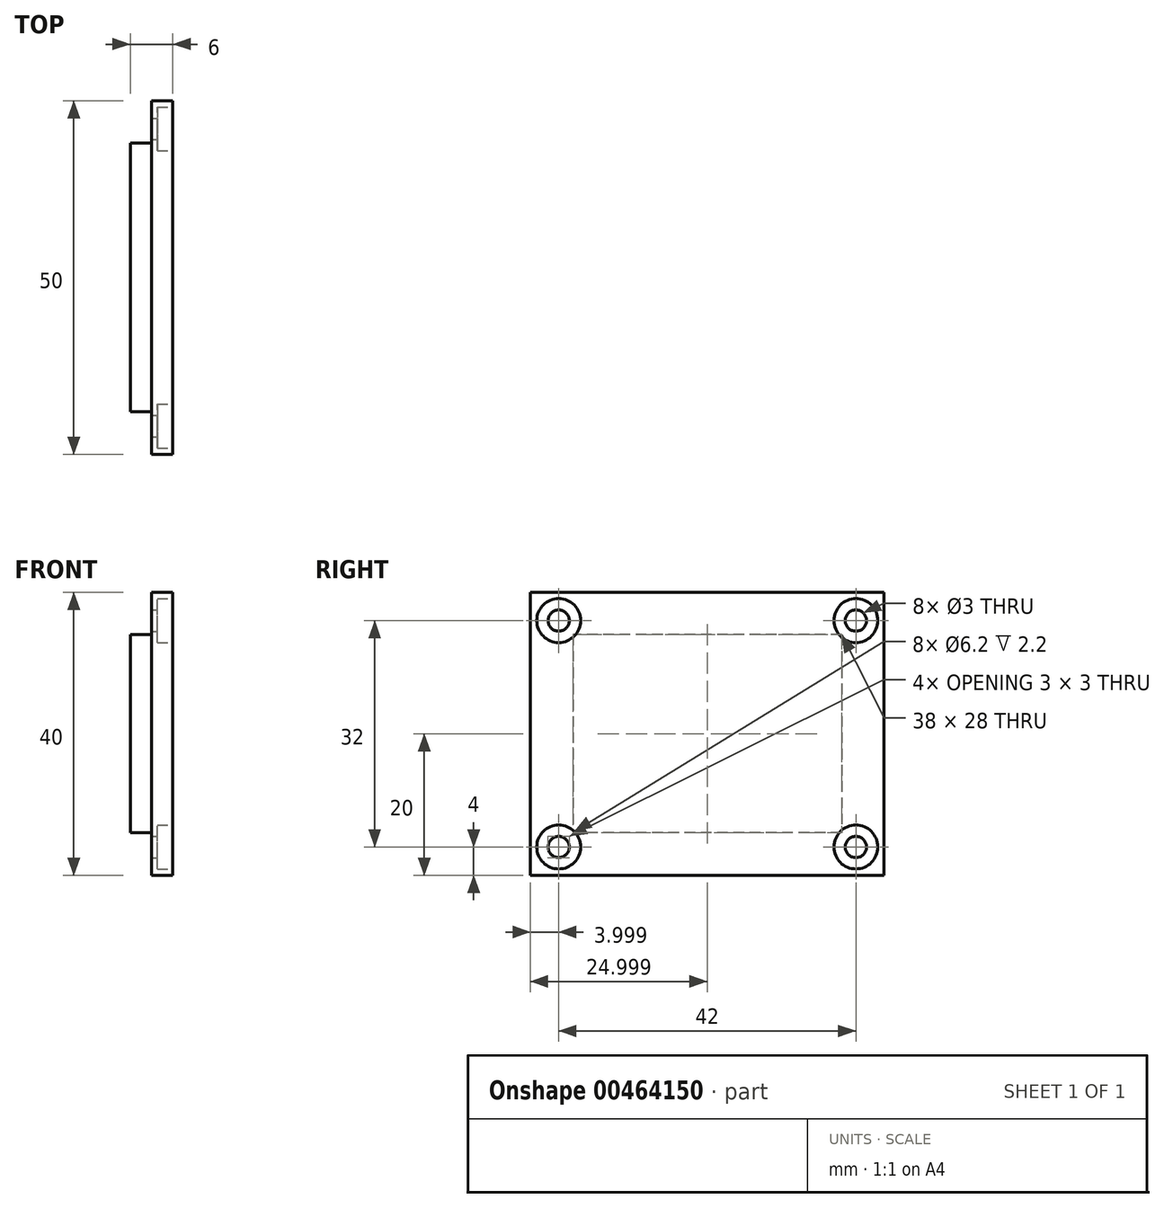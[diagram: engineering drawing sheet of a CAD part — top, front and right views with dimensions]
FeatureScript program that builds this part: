
annotation { "Feature Type Name" : "Feature", "Feature Type Description" : "" }
export const myFeature = defineFeature(function(context is Context, id is Id, definition is map)
    precondition{}
    {
        {
            var Q0;
            Q0=qCreatedBy(makeId("Right.planeOp"),FACE);
            var sketch = newSketch(context, id + "F0", { "sketchPlane" : qUnion([Q0])});
            skLineSegment(sketch, "E0.bottom", {"start": v(1.15, 0) * mm, "end": v(51.15, 0) * mm});
            skLineSegment(sketch, "E0.top", {"start": v(1.15, 40) * mm, "end": v(51.15, 40) * mm});
            skLineSegment(sketch, "E0.left", {"start": v(1.15, 0) * mm, "end": v(1.15, 40) * mm});
            skLineSegment(sketch, "E0.right", {"start": v(51.15, 0) * mm, "end": v(51.15, 40) * mm});
            skSolve(sketch);
        }
        {
            var Q0;
            Q0 = qSketchRegion(id + "F0", true);
            extrude(context, id + "F1", {"entities" : qUnion([Q0]), "depth" : 6 * mm});
        }
        {
            var Q0;
            Q0=makeQuery(id+"F1.opExtrude","CAP_FACE",FACE,{"disambiguationData":[OSD([sQuery(id+"F0.wireOp",EDGE,"E0.bottom"),sQuery(id+"F0.wireOp",EDGE,"E0.top"),sQuery(id+"F0.wireOp",EDGE,"E0.left"),sQuery(id+"F0.wireOp",EDGE,"E0.right")])],"isStart":true});
            var sketch = newSketch(context, id + "F2", { "sketchPlane" : qUnion([Q0])});
            skLineSegment(sketch, "E1.bottom", {"start": v(-45.15, 34) * mm, "end": v(-7.15, 34) * mm});
            skLineSegment(sketch, "E1.top", {"start": v(-45.15, 6) * mm, "end": v(-7.15, 6) * mm});
            skLineSegment(sketch, "E1.left", {"start": v(-45.15, 34) * mm, "end": v(-45.15, 6) * mm});
            skLineSegment(sketch, "E1.right", {"start": v(-7.15, 34) * mm, "end": v(-7.15, 6) * mm});
            skSolve(sketch);
        }
        {
            var Q0;
            Q0=makeQuery(id+"F2.imprint","IMPRINT",FACE,{"disambiguationData":[TD([[makeQuery(id+"F2.imprint","IMPRINT",EDGE,{"derivedFrom":sQuery(id+"F2.wireOp",EDGE,"E1.bottom")}),1.0]])]});
            extrude(context, id + "F3", {"entities" : qUnion([Q0]), "operationType" : NewBodyOperationType.REMOVE, "oppositeDirection" : true, "depth" : 3 * mm});
        }
        {
            var Q0;
            Q0=makeQuery(id+"F1.opExtrude","CAP_FACE",FACE,{"disambiguationData":[OSD([sQuery(id+"F0.wireOp",EDGE,"E0.bottom"),sQuery(id+"F0.wireOp",EDGE,"E0.top"),sQuery(id+"F0.wireOp",EDGE,"E0.left"),sQuery(id+"F0.wireOp",EDGE,"E0.right")])],"isStart":false});
            var sketch = newSketch(context, id + "F4", { "sketchPlane" : qUnion([Q0])});
            skCircle(sketch, "E2", {"center": v(47.15, 36) * mm, "radius": 1.5 * mm});
            skCircle(sketch, "E3", {"center": v(5.15, 36) * mm, "radius": 1.5 * mm});
            skCircle(sketch, "E4", {"center": v(5.15, 4) * mm, "radius": 1.5 * mm});
            skCircle(sketch, "E5", {"center": v(47.15, 4) * mm, "radius": 1.5 * mm});
            skSolve(sketch);
        }
        {
            var Q0;
            Q0 = qSketchRegion(id + "F4", true);
            extrude(context, id + "F5", {"entities" : qUnion([Q0]), "operationType" : NewBodyOperationType.REMOVE, "endBound" : BoundingType.THROUGH_ALL, "oppositeDirection" : true, "depth" : 25 * mm});
        }
        {
            var Q0;
            Q0=makeQuery(id+"F1.opExtrude","CAP_FACE",FACE,{"disambiguationData":[OSD([sQuery(id+"F0.wireOp",EDGE,"E0.bottom"),sQuery(id+"F0.wireOp",EDGE,"E0.top"),sQuery(id+"F0.wireOp",EDGE,"E0.left"),sQuery(id+"F0.wireOp",EDGE,"E0.right")])],"isStart":false});
            var sketch = newSketch(context, id + "F6", { "sketchPlane" : qUnion([Q0])});
            skCircle(sketch, "E6", {"center": v(5.15, 36) * mm, "radius": 3.1 * mm});
            skCircle(sketch, "E7", {"center": v(47.15, 36) * mm, "radius": 3.1 * mm});
            skCircle(sketch, "E8", {"center": v(47.15, 4) * mm, "radius": 3.1 * mm});
            skCircle(sketch, "E9", {"center": v(5.15, 4) * mm, "radius": 3.1 * mm});
            skSolve(sketch);
        }
        {
            var Q0;
            Q0 = qSketchRegion(id + "F6", true);
            extrude(context, id + "F7", {"entities" : qUnion([Q0]), "operationType" : NewBodyOperationType.REMOVE, "oppositeDirection" : true, "depth" : 2.2 * mm});
        }
        {
            var Q0;
            Q0=makeQuery(id+"F1.opExtrude","SWEPT_BODY",BODY,{"disambiguationData":[OSD([sQuery(id+"F0.wireOp",EDGE,"E0.bottom"),sQuery(id+"F0.wireOp",EDGE,"E0.top"),sQuery(id+"F0.wireOp",EDGE,"E0.left"),sQuery(id+"F0.wireOp",EDGE,"E0.right")])]});
            transform(context, id + "F8", {"entities" : qUnion([Q0]), "transformType" : TransformType.TRANSLATION_3D, "dx" : 0 * mm, "dy" : 0 * mm, "dz" : 0 * mm, "makeCopy" : true});
        }
    });
